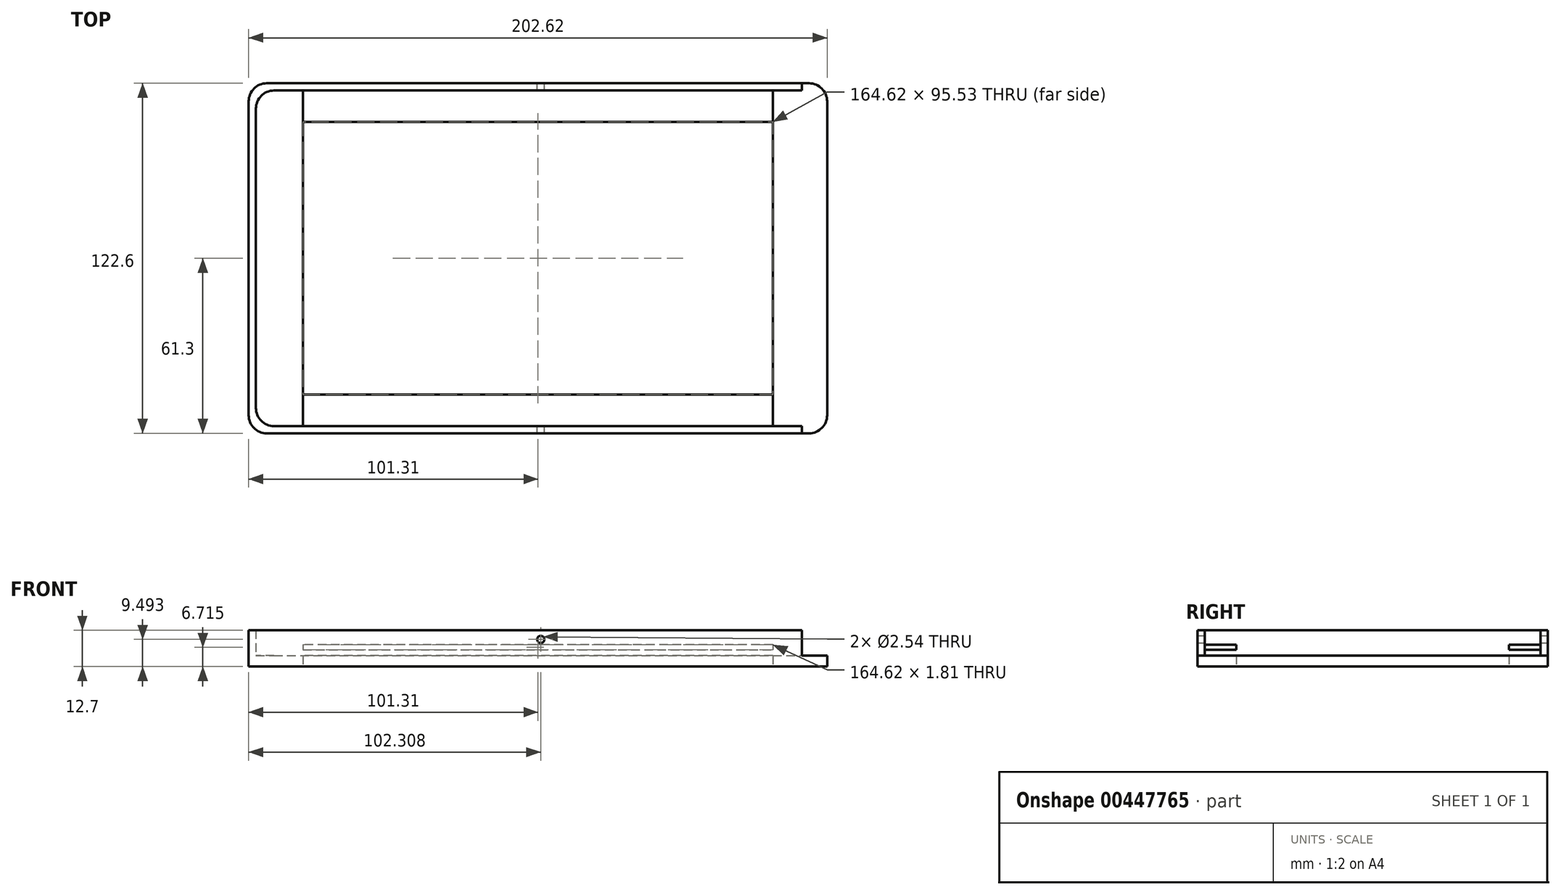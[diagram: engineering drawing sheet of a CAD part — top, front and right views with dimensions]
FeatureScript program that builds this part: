
annotation { "Feature Type Name" : "Feature", "Feature Type Description" : "" }
export const myFeature = defineFeature(function(context is Context, id is Id, definition is map)
    precondition{}
    {
        {
            var Q0;
            Q0=qCreatedBy(makeId("Top.planeOp"),FACE);
            var sketch = newSketch(context, id + "F0", { "sketchPlane" : qUnion([Q0])});
            skLineSegment(sketch, "E0.bottom", {"start": v(94.96, -61.3) * mm, "end": v(-94.96, -61.3) * mm});
            skLineSegment(sketch, "E0.top", {"start": v(94.96, 61.3) * mm, "end": v(-94.96, 61.3) * mm});
            skLineSegment(sketch, "E0.left", {"start": v(101.3, -54.95) * mm, "end": v(101.3, 54.95) * mm});
            skLineSegment(sketch, "E0.right", {"start": v(-101.3, -54.95) * mm, "end": v(-101.3, 54.95) * mm});
            skPoint(sketch, "E0.middle", {"position": v(0, 0) * mm});
            skPoint(sketch, "E1.visualSharp", {"position": v(101.3, -61.3) * mm});
            skArc(sketch, "E1.filletArc", {"start": v(94.96, -61.3) * mm, "mid": v(99.45, -59.44) * mm, "end": v(101.3, -54.95) * mm});
            skPoint(sketch, "E2.visualSharp", {"position": v(-101.3, -61.3) * mm});
            skArc(sketch, "E2.filletArc", {"start": v(-101.3, -54.95) * mm, "mid": v(-99.45, -59.44) * mm, "end": v(-94.96, -61.3) * mm});
            skPoint(sketch, "E3.visualSharp", {"position": v(-101.3, 61.3) * mm});
            skArc(sketch, "E3.filletArc", {"start": v(-94.96, 61.3) * mm, "mid": v(-99.45, 59.44) * mm, "end": v(-101.3, 54.95) * mm});
            skPoint(sketch, "E4.visualSharp", {"position": v(101.3, 61.3) * mm});
            skArc(sketch, "E4.filletArc", {"start": v(101.3, 54.95) * mm, "mid": v(99.45, 59.44) * mm, "end": v(94.96, 61.3) * mm});
            skLineSegment(sketch, "E5.0", {"start": v(-82.3, -54.95) * mm, "end": v(-82.3, 54.95) * mm});
            skLineSegment(sketch, "E6.0", {"start": v(82.3, -54.95) * mm, "end": v(-82.3, -54.95) * mm});
            skLineSegment(sketch, "E7.0", {"start": v(82.3, -54.95) * mm, "end": v(82.3, 54.95) * mm});
            skLineSegment(sketch, "E8.0", {"start": v(82.3, 54.95) * mm, "end": v(-82.3, 54.95) * mm});
            skSolve(sketch);
        }
        {
            var Q0;
            Q0=makeQuery(id+"F0.imprint","IMPRINT",FACE,{"disambiguationData":[TD([[makeQuery(id+"F0.imprint","IMPRINT",EDGE,{"derivedFrom":sQuery(id+"F0.wireOp",EDGE,"E0.bottom")}),-1.0]])]});
            extrude(context, id + "F1", {"entities" : qUnion([Q0]), "depth" : 3.8 * mm});
        }
        {
            var Q0;
            Q0=qCreatedBy(makeId("Top.planeOp"),FACE);
            var sketch = newSketch(context, id + "F2", { "sketchPlane" : qUnion([Q0])});
            skLineSegment(sketch, "E9.bottom", {"start": v(82.3, 58.76) * mm, "end": v(-82.3, 58.76) * mm});
            skLineSegment(sketch, "E9.top", {"start": v(82.3, 47.76) * mm, "end": v(-82.3, 47.76) * mm});
            skLineSegment(sketch, "E9.left", {"start": v(82.3, 58.76) * mm, "end": v(82.3, 47.76) * mm});
            skLineSegment(sketch, "E9.right", {"start": v(-82.3, 58.76) * mm, "end": v(-82.3, 47.76) * mm});
            skSolve(sketch);
        }
        {
            var Q0;
            Q0=makeQuery(id+"F2.imprint","IMPRINT",FACE,{"disambiguationData":[TD([[makeQuery(id+"F2.imprint","IMPRINT",EDGE,{"derivedFrom":sQuery(id+"F2.wireOp",EDGE,"E9.bottom")}),1.0]])]});
            extrude(context, id + "F3", {"entities" : qUnion([Q0]), "operationType" : NewBodyOperationType.ADD, "depth" : 7.62 * mm});
        }
        {
            var Q0;
            Q0=makeQuery(id+"F3.opExtrude","SWEPT_FACE",FACE,{"disambiguationData":[OSD([sQuery(id+"F2.wireOp",EDGE,"E9.top")])]});
            var sketch = newSketch(context, id + "F4", { "sketchPlane" : qUnion([Q0])});
            skLineSegment(sketch, "E10.bottom", {"start": v(-82.3, 5.81) * mm, "end": v(82.3, 5.81) * mm});
            skLineSegment(sketch, "E10.top", {"start": v(-82.3, 3.81) * mm, "end": v(82.3, 3.81) * mm});
            skLineSegment(sketch, "E10.left", {"start": v(-82.3, 5.81) * mm, "end": v(-82.3, 3.81) * mm});
            skLineSegment(sketch, "E10.right", {"start": v(82.3, 5.81) * mm, "end": v(82.3, 3.81) * mm});
            skSolve(sketch);
        }
        {
            var Q0;
            Q0=makeQuery(id+"F4.imprint","IMPRINT",FACE,{"disambiguationData":[TD([[makeQuery(id+"F4.imprint","IMPRINT",EDGE,{"derivedFrom":sQuery(id+"F4.wireOp",EDGE,"E10.bottom")}),-1.0]])]});
            extrude(context, id + "F5", {"entities" : qUnion([Q0]), "operationType" : NewBodyOperationType.REMOVE, "oppositeDirection" : true, "depth" : 11 * mm});
        }
        {
            var Q0;
            Q0=makeQuery(id+"F3.boolean.opBoolean","MERGE",FACE,{"derivedFrom":[makeQuery(id+"F1.opExtrude","CAP_FACE",FACE,{"disambiguationData":[OSD([sQuery(id+"F0.wireOp",EDGE,"E0.bottom"),sQuery(id+"F0.wireOp",EDGE,"E0.top"),sQuery(id+"F0.wireOp",EDGE,"E0.left"),sQuery(id+"F0.wireOp",EDGE,"E0.right"),sQuery(id+"F0.wireOp",EDGE,"E1.filletArc"),sQuery(id+"F0.wireOp",EDGE,"E2.filletArc"),sQuery(id+"F0.wireOp",EDGE,"E3.filletArc"),sQuery(id+"F0.wireOp",EDGE,"E4.filletArc"),sQuery(id+"F0.wireOp",EDGE,"E5.0"),sQuery(id+"F0.wireOp",EDGE,"E6.0"),sQuery(id+"F0.wireOp",EDGE,"E7.0"),sQuery(id+"F0.wireOp",EDGE,"E8.0")])],"isStart":true}),makeQuery(id+"F3.opExtrude","CAP_FACE",FACE,{"disambiguationData":[OSD([sQuery(id+"F2.wireOp",EDGE,"E9.bottom"),sQuery(id+"F2.wireOp",EDGE,"E9.top"),sQuery(id+"F2.wireOp",EDGE,"E9.left"),sQuery(id+"F2.wireOp",EDGE,"E9.right")])],"isStart":true})]});
            var sketch = newSketch(context, id + "F6", { "sketchPlane" : qUnion([Q0])});
            skLineSegment(sketch, "E11.bottom", {"start": v(82.3, 58.76) * mm, "end": v(-82.3, 58.76) * mm});
            skLineSegment(sketch, "E11.top", {"start": v(82.3, 47.76) * mm, "end": v(-82.3, 47.76) * mm});
            skLineSegment(sketch, "E11.left", {"start": v(82.3, 58.76) * mm, "end": v(82.3, 47.76) * mm});
            skLineSegment(sketch, "E11.right", {"start": v(-82.3, 58.76) * mm, "end": v(-82.3, 47.76) * mm});
            skSolve(sketch);
        }
        {
            var Q0;
            Q0=qSketchRegion(id+"F6",true);
            extrude(context, id + "F7", {"entities" : qUnion([Q0]), "operationType" : NewBodyOperationType.ADD, "oppositeDirection" : true, "depth" : 7.62 * mm});
        }
        {
            var Q0;
            Q0=makeQuery(id+"F7.opExtrude","SWEPT_FACE",FACE,{"disambiguationData":[OSD([sQuery(id+"F6.wireOp",EDGE,"E11.top")])]});
            var sketch = newSketch(context, id + "F8", { "sketchPlane" : qUnion([Q0])});
            skLineSegment(sketch, "E12.bottom", {"start": v(-82.3, 5.81) * mm, "end": v(82.3, 5.81) * mm});
            skLineSegment(sketch, "E12.top", {"start": v(-82.3, 3.81) * mm, "end": v(82.3, 3.81) * mm});
            skLineSegment(sketch, "E12.left", {"start": v(-82.3, 5.81) * mm, "end": v(-82.3, 3.81) * mm});
            skLineSegment(sketch, "E12.right", {"start": v(82.3, 5.81) * mm, "end": v(82.3, 3.81) * mm});
            skSolve(sketch);
        }
        {
            var Q0;
            Q0=makeQuery(id+"F8.imprint","IMPRINT",FACE,{"disambiguationData":[TD([[makeQuery(id+"F8.imprint","IMPRINT",EDGE,{"derivedFrom":sQuery(id+"F8.wireOp",EDGE,"E12.bottom")}),-1.0]])]});
            extrude(context, id + "F9", {"entities" : qUnion([Q0]), "operationType" : NewBodyOperationType.REMOVE, "oppositeDirection" : true, "depth" : 11 * mm});
        }
        {
            var Q0;
            Q0=qCreatedBy(makeId("Top.planeOp"),FACE);
            var sketch = newSketch(context, id + "F10", { "sketchPlane" : qUnion([Q0])});
            skLineSegment(sketch, "E13.bottom", {"start": v(92.42, -61.3) * mm, "end": v(-94.96, -61.3) * mm});
            skLineSegment(sketch, "E13.top", {"start": v(94.96, 61.3) * mm, "end": v(-94.96, 61.3) * mm});
            skLineSegment(sketch, "E13.right", {"start": v(-101.3, -54.95) * mm, "end": v(-101.3, 54.95) * mm});
            skPoint(sketch, "E13.middle", {"position": v(0, 0) * mm});
            skPoint(sketch, "E14.visualSharp", {"position": v(101.3, -61.3) * mm});
            skArc(sketch, "E14.filletArc", {"start": v(92.42, -61.3) * mm, "mid": v(96.9, -59.44) * mm, "end": v(98.77, -54.95) * mm});
            skPoint(sketch, "E15.visualSharp", {"position": v(-101.3, -61.3) * mm});
            skArc(sketch, "E15.filletArc", {"start": v(-101.3, -54.95) * mm, "mid": v(-99.45, -59.44) * mm, "end": v(-94.96, -61.3) * mm});
            skPoint(sketch, "E16.visualSharp", {"position": v(-101.3, 61.3) * mm});
            skArc(sketch, "E16.filletArc", {"start": v(-94.96, 61.3) * mm, "mid": v(-99.45, 59.44) * mm, "end": v(-101.3, 54.95) * mm});
            skPoint(sketch, "E17.visualSharp", {"position": v(101.3, 61.3) * mm});
            skArc(sketch, "E17.filletArc", {"start": v(101.3, 54.95) * mm, "mid": v(99.45, 59.44) * mm, "end": v(94.96, 61.3) * mm});
            skLineSegment(sketch, "E18.0", {"start": v(-98.77, -50.97) * mm, "end": v(-98.77, 52.42) * mm});
            skLineSegment(sketch, "E19.0", {"start": v(92.42, -58.76) * mm, "end": v(-92.42, -58.76) * mm});
            skLineSegment(sketch, "E20.0", {"start": v(94.96, 58.76) * mm, "end": v(-92.42, 58.76) * mm});
            skLineSegment(sketch, "E21", {"start": v(94.96, 58.76) * mm, "end": v(101.3, 54.95) * mm});
            skLineSegment(sketch, "E22", {"start": v(98.77, -54.95) * mm, "end": v(92.42, -58.76) * mm});
            skPoint(sketch, "E23", {"position": v(-94.96, -58.76) * mm});
            skPoint(sketch, "E24", {"position": v(-98.77, -54.95) * mm});
            skLineSegment(sketch, "E25", {"start": v(-98.77, -50.97) * mm, "end": v(-98.77, -52.41) * mm});
            skPoint(sketch, "E26", {"position": v(-92.42, 58.76) * mm});
            skPoint(sketch, "E27", {"position": v(-98.77, 52.41) * mm});
            skPoint(sketch, "E28", {"position": v(-92.42, 52.41) * mm});
            skArc(sketch, "E29", {"start": v(-92.42, 58.76) * mm, "mid": v(-96.9, 56.9) * mm, "end": v(-98.77, 52.41) * mm});
            skPoint(sketch, "E30.orphan", {"position": v(-94.96, 58.76) * mm});
            skPoint(sketch, "E31.orphan", {"position": v(-98.77, 54.95) * mm});
            skPoint(sketch, "E32", {"position": v(-92.42, -52.41) * mm});
            skPoint(sketch, "E33.orphan", {"position": v(-92.42, -61.3) * mm});
            skArc(sketch, "E34", {"start": v(-98.77, -52.41) * mm, "mid": v(-96.9, -56.9) * mm, "end": v(-92.42, -58.76) * mm});
            skSolve(sketch);
        }
        {
            var Q0;
            Q0=qSketchRegion(id+"F10",true);
            extrude(context, id + "F11", {"entities" : qUnion([Q0]), "operationType" : NewBodyOperationType.ADD, "depth" : 12.7 * mm});
        }
        {
            var Q0;
            Q0=makeQuery(id+"F11.boolean.opBoolean","MERGE",FACE,{"derivedFrom":[makeQuery(id+"F1.opExtrude","SWEPT_FACE",FACE,{"disambiguationData":[OSD([sQuery(id+"F0.wireOp",EDGE,"E0.bottom")])]}),makeQuery(id+"F11.opExtrude","SWEPT_FACE",FACE,{"disambiguationData":[OSD([sQuery(id+"F10.wireOp",EDGE,"E13.bottom")])]})]});
            var sketch = newSketch(context, id + "F12", { "sketchPlane" : qUnion([Q0])});
            skLineSegment(sketch, "E35.bottom", {"start": v(92.42, 12.7) * mm, "end": v(106.23, 12.7) * mm});
            skLineSegment(sketch, "E35.top", {"start": v(92.42, 3.81) * mm, "end": v(106.23, 3.81) * mm});
            skLineSegment(sketch, "E35.left", {"start": v(92.42, 12.7) * mm, "end": v(92.42, 3.81) * mm});
            skLineSegment(sketch, "E35.right", {"start": v(106.23, 12.7) * mm, "end": v(106.23, 3.81) * mm});
            skSolve(sketch);
        }
        {
            var Q0;
            Q0=makeQuery(id+"F12.imprint","IMPRINT",FACE,{"disambiguationData":[TD([[makeQuery(id+"F12.imprint","IMPRINT",EDGE,{"derivedFrom":sQuery(id+"F12.wireOp",EDGE,"E35.bottom")}),-1.0]])]});
            extrude(context, id + "F13", {"entities" : qUnion([Q0]), "operationType" : NewBodyOperationType.REMOVE, "oppositeDirection" : true, "depth" : 127 * mm});
        }
        {
            var Q0;
            Q0=makeQuery(id+"F11.boolean.opBoolean","MERGE",FACE,{"derivedFrom":[makeQuery(id+"F1.opExtrude","SWEPT_FACE",FACE,{"disambiguationData":[OSD([sQuery(id+"F0.wireOp",EDGE,"E0.top")])]}),makeQuery(id+"F11.opExtrude","SWEPT_FACE",FACE,{"disambiguationData":[OSD([sQuery(id+"F10.wireOp",EDGE,"E13.top")])]})]});
            var sketch = newSketch(context, id + "F14", { "sketchPlane" : qUnion([Q0])});
            skPoint(sketch, "E36", {"position": v(0, 6.35) * mm});
            skPoint(sketch, "E36.positionSnap0", {"position": v(94.96, 6.35) * mm});
            skPoint(sketch, "E37", {"position": v(0, 9.5) * mm});
            skPoint(sketch, "E38", {"position": v(-1, 9.5) * mm});
            skSolve(sketch);
        }
        {
            var Q0;
            Q0=sQuery(id+"F14.wireOp",VERTEX,"E38");
            var Q1;
            Q1=makeQuery(id+"F5.boolean.opBoolean","SPLIT",BODY,{"disambiguationData":[OD(1.0)],"derivedFrom":makeQuery(id+"F1.opExtrude","SWEPT_BODY",BODY,{"disambiguationData":[OSD([sQuery(id+"F0.wireOp",EDGE,"E0.bottom"),sQuery(id+"F0.wireOp",EDGE,"E0.top"),sQuery(id+"F0.wireOp",EDGE,"E0.left"),sQuery(id+"F0.wireOp",EDGE,"E0.right"),sQuery(id+"F0.wireOp",EDGE,"E1.filletArc"),sQuery(id+"F0.wireOp",EDGE,"E2.filletArc"),sQuery(id+"F0.wireOp",EDGE,"E3.filletArc"),sQuery(id+"F0.wireOp",EDGE,"E4.filletArc"),sQuery(id+"F0.wireOp",EDGE,"E5.0"),sQuery(id+"F0.wireOp",EDGE,"E6.0"),sQuery(id+"F0.wireOp",EDGE,"E7.0"),sQuery(id+"F0.wireOp",EDGE,"E8.0")])]})});
            hole(context, id + "F15", {"style" : HoleStyle.SIMPLE, "endStyle" : HoleEndStyle.THROUGH, "holeDiameter" : 2.54 * mm, "tappedDepth" : 12.7 * mm, "tapClearance" : 3, "startFromSketch" : true, "locations" : qUnion([Q0]), "scope" : qUnion([Q1])});
        }
    });
